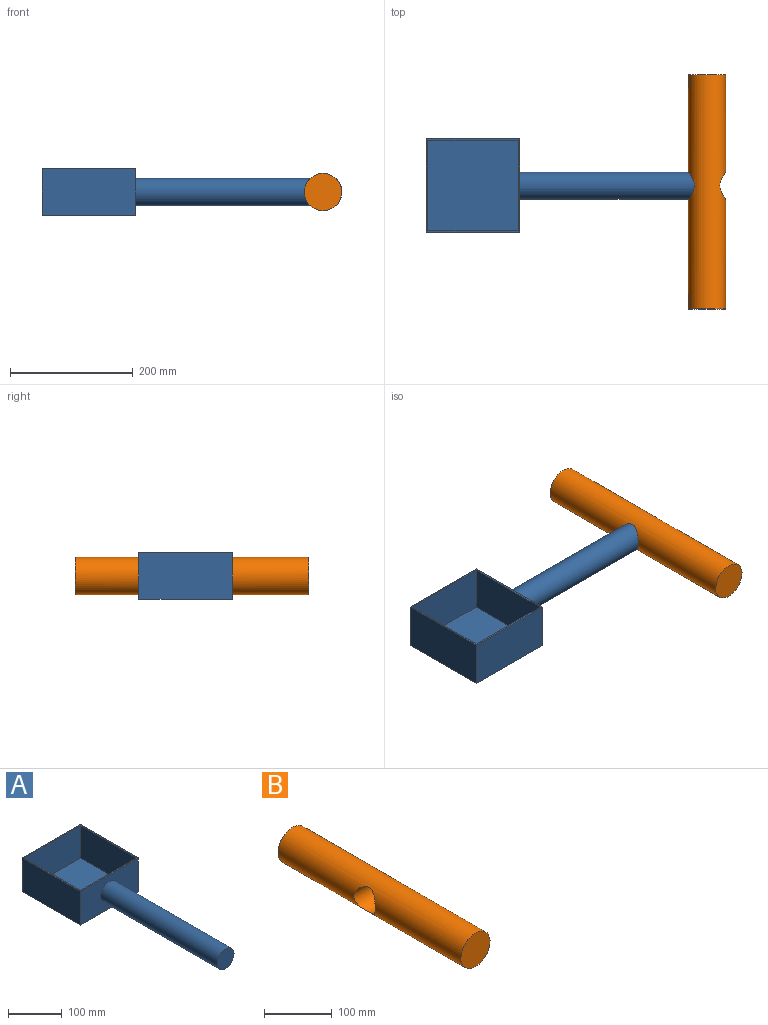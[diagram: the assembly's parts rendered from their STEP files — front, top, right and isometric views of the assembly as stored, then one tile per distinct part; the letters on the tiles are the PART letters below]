
ASSEMBLY  parts=2 mates=1
PART A: 13 faces, bbox 152.4x457.2x76.2 mm
  f0: plane 152.4x152.4mm, normal (0,0,1), area 1522.6mm2, adj f1,f2,f3,f4,f6,f7,f8,f9
  f1: plane 152.4x76.2mm, normal (0,-1,0), area 10061.1mm2, adj f0,f2,f4,f5,f11
  f2: plane 152.4x76.2mm, normal (1,0,0), area 11612.9mm2, adj f0,f1,f3,f5
  f3: plane 152.4x76.2mm, normal (0,1,0), area 11612.9mm2, adj f0,f2,f4,f5
  f4: plane 152.4x76.2mm, normal (-1,0,0), area 11612.9mm2, adj f0,f1,f3,f5
  f5: plane 152.4x152.4mm, normal (0,0,-1), area 23225.8mm2, adj f1,f2,f3,f4
  f6: plane 147.32x73.66mm, normal (0,1,0), area 10851.6mm2, adj f0,f7,f9,f10
  f7: plane 147.32x73.66mm, normal (-1,0,0), area 10851.6mm2, adj f0,f6,f8,f10
  f8: plane 147.32x73.66mm, normal (0,-1,0), area 10851.6mm2, adj f0,f7,f9,f10
  f9: plane 147.32x73.66mm, normal (1,0,0), area 10851.6mm2, adj f0,f6,f8,f10
  f10: plane 147.32x147.32mm, normal (0,0,1), area 21703.2mm2, adj f6,f7,f8,f9
  f11: cylinder r=22.23mm len=304.8mm, axis (0,1,0), area 42563.4mm2, adj f1,f12
  f12: plane 44.45x44.45mm, normal (0,-1,0), area 1551.8mm2, adj f11
PART B: 4 faces, bbox 60.6x381x60.6 mm
  f0: cylinder r=30.3mm len=381mm, axis (0,1,0), area 69153.5mm2, adj f1,f2,f3
  f1: plane 60.59x60.59mm, normal (0,-1,0), area 2883.6mm2, adj f0
  f2: plane 60.59x60.59mm, normal (0,1,0), area 2883.6mm2, adj f0
  f3: cylinder r=22.23mm len=60.59mm, axis (1,0,0), area 7170.7mm2, adj f0
PLACE A rot(axis=(0,0,1),90deg) t=(-387.7,-166.33,164.73)mm
PLACE B t=(-6.7,13.85,202.83)mm fixed
MATE fastened A.f11 <-> B.f3  axis (1,0,0) through (-6.7,-166.33,202.83)mm
